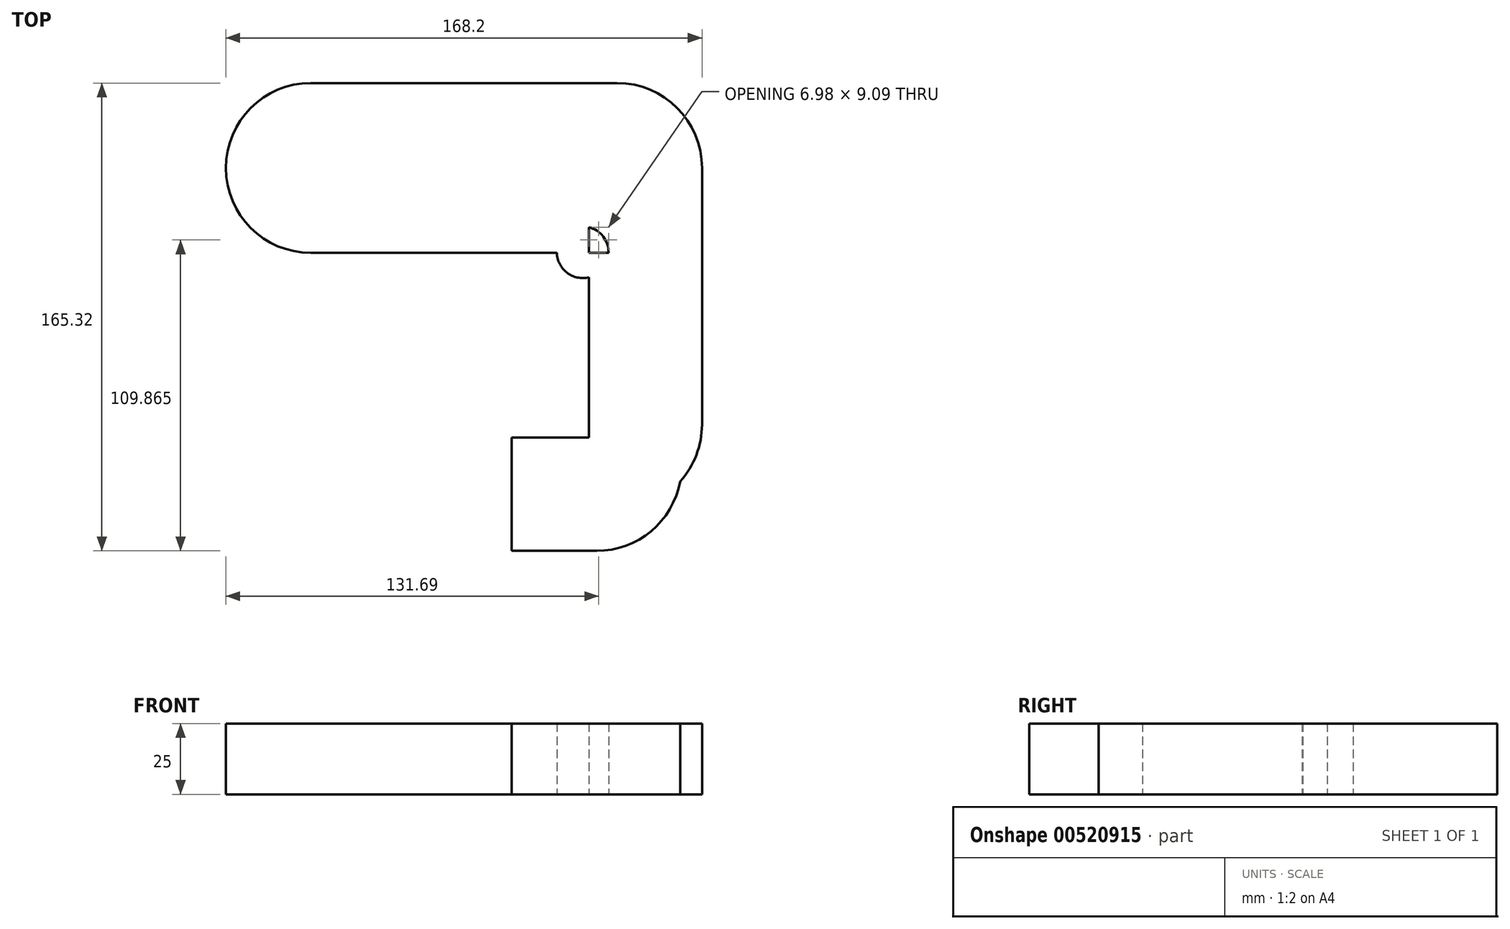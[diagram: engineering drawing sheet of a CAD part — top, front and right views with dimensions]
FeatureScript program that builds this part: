
annotation { "Feature Type Name" : "Feature", "Feature Type Description" : "" }
export const myFeature = defineFeature(function(context is Context, id is Id, definition is map)
    precondition{}
    {
        {
            var Q0;
            Q0=qCreatedBy(makeId("Top.planeOp"),FACE);
            var sketch = newSketch(context, id + "F0", { "sketchPlane" : qUnion([Q0])});
            skLineSegment(sketch, "E0.bottom", {"start": v(54.1, 30) * mm, "end": v(-54.1, 30) * mm});
            skLineSegment(sketch, "E0.top", {"start": v(84.1, -30) * mm, "end": v(-54.1, -30) * mm});
            skLineSegment(sketch, "E0.left", {"start": v(84.1, 0) * mm, "end": v(84.1, -30) * mm});
            skLineSegment(sketch, "E0.right", {"start": v(-84.1, 0) * mm, "end": v(-84.1, 0) * mm});
            skPoint(sketch, "E0.middle", {"position": v(0, 0) * mm});
            skLineSegment(sketch, "E1.bottom", {"start": v(44.1, 30) * mm, "end": v(54.1, 30) * mm});
            skLineSegment(sketch, "E1.top", {"start": v(44.1, -120.68) * mm, "end": v(54.1, -120.68) * mm});
            skLineSegment(sketch, "E1.left", {"start": v(44.1, 30) * mm, "end": v(44.1, -120.68) * mm});
            skLineSegment(sketch, "E1.right", {"start": v(84.1, 0) * mm, "end": v(84.1, -90.68) * mm});
            skPoint(sketch, "E2.visualSharp", {"position": v(84.1, 30) * mm});
            skArc(sketch, "E2.filletArc", {"start": v(84.1, 0) * mm, "mid": v(75.31, 21.21) * mm, "end": v(54.1, 30) * mm});
            skLineSegment(sketch, "E3.bottom", {"start": v(76.89, -95.32) * mm, "end": v(16.89, -95.32) * mm});
            skLineSegment(sketch, "E3.top", {"start": v(46.89, -135.32) * mm, "end": v(16.89, -135.32) * mm});
            skLineSegment(sketch, "E3.left", {"start": v(76.89, -95.32) * mm, "end": v(76.89, -105.32) * mm});
            skLineSegment(sketch, "E3.right", {"start": v(16.89, -95.32) * mm, "end": v(16.89, -135.32) * mm});
            skPoint(sketch, "E4.visualSharp", {"position": v(-84.1, 30) * mm});
            skArc(sketch, "E4.filletArc", {"start": v(-54.1, 30) * mm, "mid": v(-75.31, 21.21) * mm, "end": v(-84.1, 0) * mm});
            skPoint(sketch, "E5.visualSharp", {"position": v(-84.1, -30) * mm});
            skArc(sketch, "E5.filletArc", {"start": v(-84.1, 0) * mm, "mid": v(-75.31, -21.21) * mm, "end": v(-54.1, -30) * mm});
            skPoint(sketch, "E6.visualSharp", {"position": v(84.1, -120.68) * mm});
            skArc(sketch, "E6.filletArc", {"start": v(54.1, -120.68) * mm, "mid": v(75.31, -111.89) * mm, "end": v(84.1, -90.68) * mm});
            skPoint(sketch, "E7.visualSharp", {"position": v(76.89, -135.32) * mm});
            skArc(sketch, "E7.filletArc", {"start": v(46.89, -135.32) * mm, "mid": v(68.1, -126.53) * mm, "end": v(76.89, -105.32) * mm});
            skPoint(sketch, "E8.first.point", {"position": v(36.67, -37.22) * mm});
            skPoint(sketch, "E8.second.point", {"position": v(51.08, -21.02) * mm});
            skPoint(sketch, "E8.third.point", {"position": v(39.4, -19.03) * mm});
            skCircle(sketch, "E9", {"center": v(41.96, -29.78) * mm, "radius": 9.12 * mm});
            skPoint(sketch, "E9.second.point", {"position": v(51.08, -30) * mm});
            skPoint(sketch, "E9.third.point", {"position": v(39.4, -21.02) * mm});
            skSolve(sketch);
        }
        {
            var Q0;
            Q0 = qSketchRegion(id + "F0", true);
            extrude(context, id + "F1", {"entities" : qUnion([Q0]), "endBound" : BoundingType.SYMMETRIC, "depth" : 25 * mm, "offsetDistance" : 25 * mm});
        }
    });
